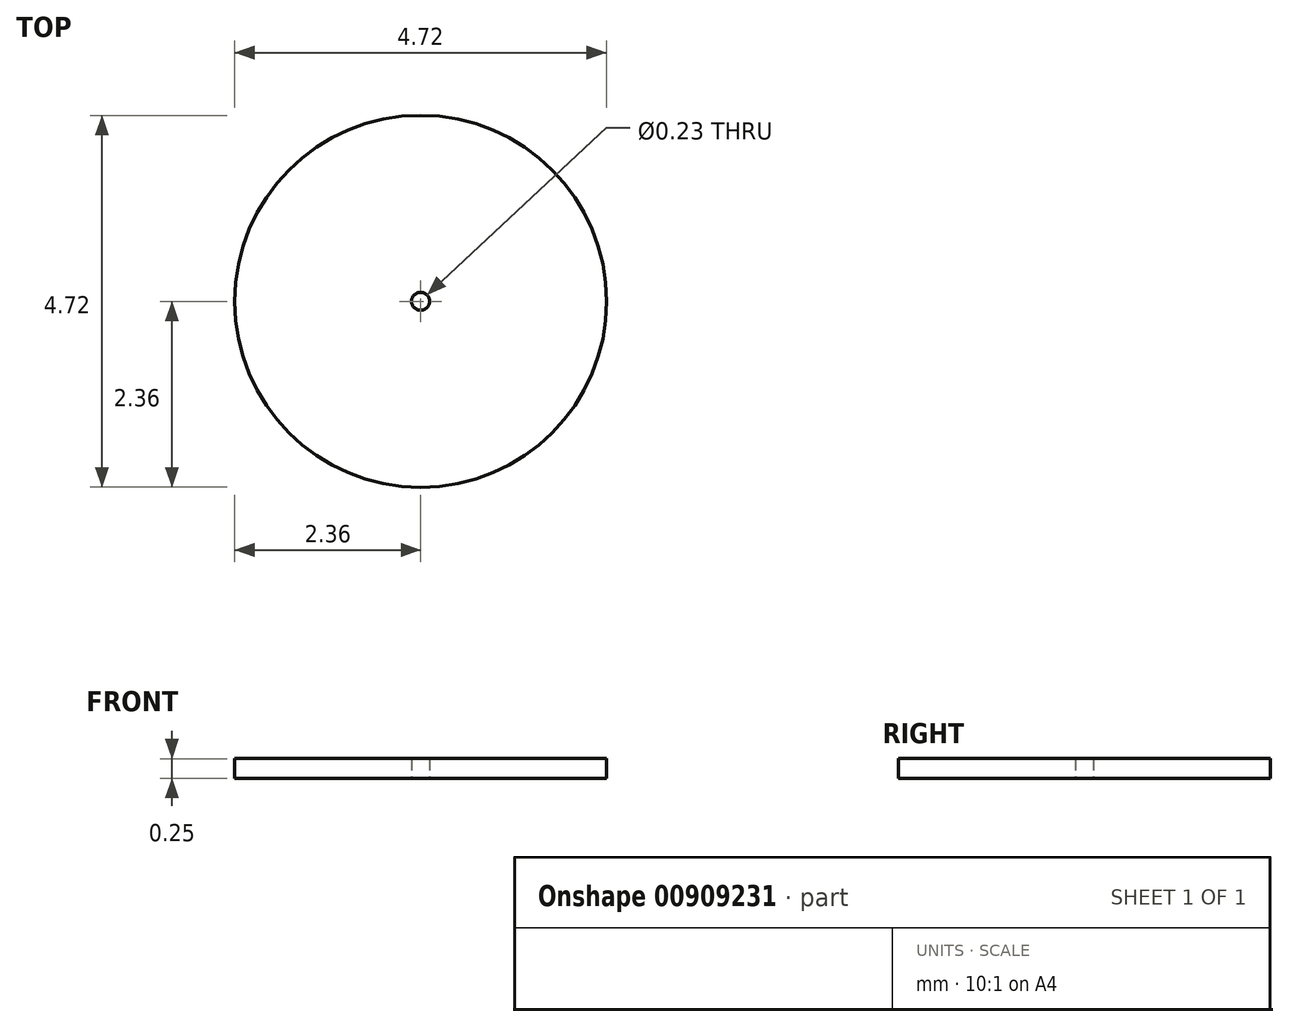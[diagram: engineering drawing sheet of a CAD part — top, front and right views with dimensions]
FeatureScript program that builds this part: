
annotation { "Feature Type Name" : "Feature", "Feature Type Description" : "" }
export const myFeature = defineFeature(function(context is Context, id is Id, definition is map)
    precondition{}
    {
        {
            var Q0;
            Q0=qCreatedBy(makeId("Top.planeOp"),FACE);
            var sketch = newSketch(context, id + "F0", { "sketchPlane" : qUnion([Q0])});
            skCircle(sketch, "E0", {"center": v(0, 0) * mm, "radius": 2.36 * mm});
            skCircle(sketch, "E1", {"center": v(0, 0) * mm, "radius": 0.11 * mm});
            skSolve(sketch);
        }
        {
            var Q0;
            Q0=makeQuery(id+"F0.imprint","IMPRINT",FACE,{"disambiguationData":[TD([[makeQuery(id+"F0.imprint","IMPRINT",EDGE,{"derivedFrom":sQuery(id+"F0.wireOp",EDGE,"E0")}),1.0]])]});
            extrude(context, id + "F1", {"entities" : qUnion([Q0]), "depth" : 0.25 * mm, "offsetDistance" : 25.4 * mm});
        }
    });
